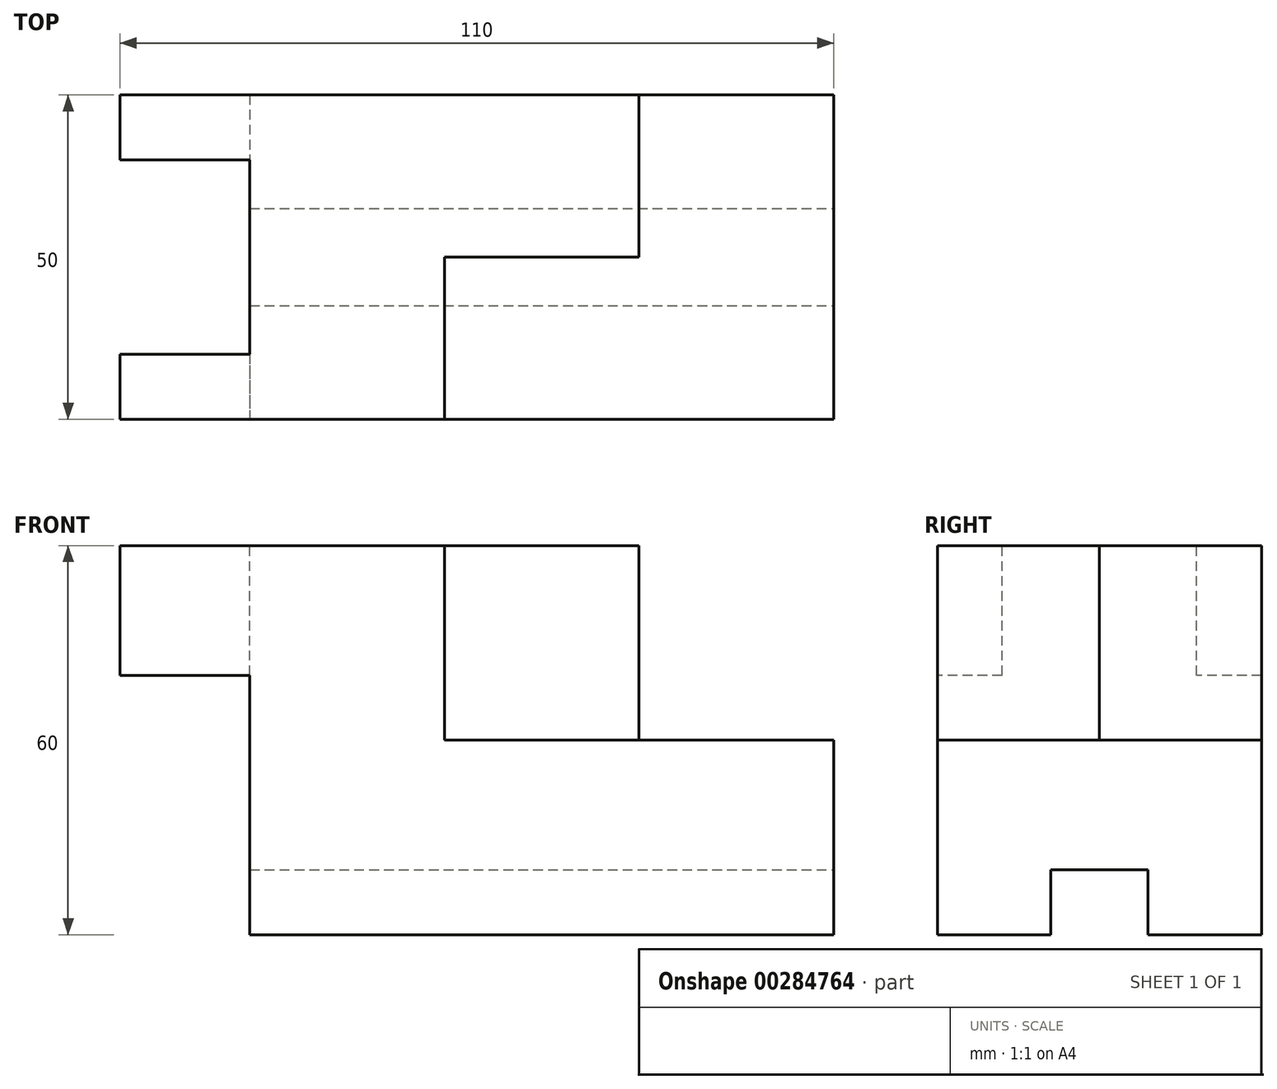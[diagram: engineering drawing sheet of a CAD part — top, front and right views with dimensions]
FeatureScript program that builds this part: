
annotation { "Feature Type Name" : "Feature", "Feature Type Description" : "" }
export const myFeature = defineFeature(function(context is Context, id is Id, definition is map)
    precondition{}
    {
        {
            var Q0;
            Q0=qCreatedBy(makeId("Top.planeOp"),FACE);
            var sketch = newSketch(context, id + "F0", { "sketchPlane" : qUnion([Q0])});
            skLineSegment(sketch, "E0.bottom", {"start": v(-55, -25) * mm, "end": v(55, -25) * mm});
            skLineSegment(sketch, "E0.top", {"start": v(-55, 25) * mm, "end": v(55, 25) * mm});
            skLineSegment(sketch, "E0.left", {"start": v(-55, -25) * mm, "end": v(-55, 25) * mm});
            skLineSegment(sketch, "E0.right", {"start": v(55, -25) * mm, "end": v(55, 25) * mm});
            skPoint(sketch, "E0.middle", {"position": v(0, 0) * mm});
            skSolve(sketch);
        }
        {
            var Q0;
            Q0 = qSketchRegion(id + "F0", true);
            extrude(context, id + "F1", {"entities" : qUnion([Q0]), "depth" : 60 * mm});
        }
        {
            var Q0;
            Q0=makeQuery(id+"F1.opExtrude","SWEPT_FACE",FACE,{"disambiguationData":[OSD([sQuery(id+"F0.wireOp",EDGE,"E0.right")])]});
            var sketch = newSketch(context, id + "F2", { "sketchPlane" : qUnion([Q0])});
            skLineSegment(sketch, "E1.bottom", {"start": v(-7.5, 10) * mm, "end": v(7.5, 10) * mm});
            skLineSegment(sketch, "E1.top", {"start": v(-7.5, -10) * mm, "end": v(7.5, -10) * mm});
            skLineSegment(sketch, "E1.left", {"start": v(-7.5, 10) * mm, "end": v(-7.5, -10) * mm});
            skLineSegment(sketch, "E1.right", {"start": v(7.5, 10) * mm, "end": v(7.5, -10) * mm});
            skPoint(sketch, "E1.middle", {"position": v(0, 0) * mm});
            skSolve(sketch);
        }
        {
            var Q0;
            Q0 = qSketchRegion(id + "F2", true);
            extrude(context, id + "F3", {"entities" : qUnion([Q0]), "operationType" : NewBodyOperationType.REMOVE, "endBound" : BoundingType.THROUGH_ALL, "oppositeDirection" : true, "depth" : 25 * mm});
        }
        {
            var Q0;
            Q0=makeQuery(id+"F1.opExtrude","CAP_FACE",FACE,{"disambiguationData":[OSD([sQuery(id+"F0.wireOp",EDGE,"E0.bottom"),sQuery(id+"F0.wireOp",EDGE,"E0.top"),sQuery(id+"F0.wireOp",EDGE,"E0.left"),sQuery(id+"F0.wireOp",EDGE,"E0.right")])],"isStart":false});
            var sketch = newSketch(context, id + "F4", { "sketchPlane" : qUnion([Q0])});
            skLineSegment(sketch, "E2", {"start": v(25, 25) * mm, "end": v(25, 0) * mm});
            skLineSegment(sketch, "E3", {"start": v(25, 0) * mm, "end": v(-5, 0) * mm});
            skLineSegment(sketch, "E4", {"start": v(-5, 0) * mm, "end": v(-5, -25) * mm});
            skLineSegment(sketch, "E5", {"start": v(-5, -25) * mm, "end": v(55, -25) * mm});
            skLineSegment(sketch, "E6", {"start": v(55, -25) * mm, "end": v(55, 25) * mm});
            skLineSegment(sketch, "E7", {"start": v(25, 25) * mm, "end": v(55, 25) * mm});
            skSolve(sketch);
        }
        {
            var Q0;
            Q0 = qSketchRegion(id + "F4", true);
            extrude(context, id + "F5", {"entities" : qUnion([Q0]), "operationType" : NewBodyOperationType.REMOVE, "oppositeDirection" : true, "depth" : 30 * mm});
        }
        {
            var Q0;
            Q0=makeQuery(id+"F1.opExtrude","SWEPT_FACE",FACE,{"disambiguationData":[OSD([sQuery(id+"F0.wireOp",EDGE,"E0.bottom")])]});
            var sketch = newSketch(context, id + "F6", { "sketchPlane" : qUnion([Q0])});
            skLineSegment(sketch, "E8.bottom", {"start": v(-55, 0) * mm, "end": v(-35, 0) * mm});
            skLineSegment(sketch, "E8.top", {"start": v(-55, 40) * mm, "end": v(-35, 40) * mm});
            skLineSegment(sketch, "E8.left", {"start": v(-55, 0) * mm, "end": v(-55, 40) * mm});
            skLineSegment(sketch, "E8.right", {"start": v(-35, 0) * mm, "end": v(-35, 40) * mm});
            skSolve(sketch);
        }
        {
            var Q0;
            Q0 = qSketchRegion(id + "F6", true);
            extrude(context, id + "F7", {"entities" : qUnion([Q0]), "operationType" : NewBodyOperationType.REMOVE, "endBound" : BoundingType.THROUGH_ALL, "oppositeDirection" : true, "depth" : 25 * mm});
        }
        {
            var Q0;
            Q0=makeQuery(id+"F1.opExtrude","CAP_FACE",FACE,{"disambiguationData":[OSD([sQuery(id+"F0.wireOp",EDGE,"E0.bottom"),sQuery(id+"F0.wireOp",EDGE,"E0.top"),sQuery(id+"F0.wireOp",EDGE,"E0.left"),sQuery(id+"F0.wireOp",EDGE,"E0.right")])],"isStart":false});
            var sketch = newSketch(context, id + "F8", { "sketchPlane" : qUnion([Q0])});
            skLineSegment(sketch, "E9.bottom", {"start": v(-35, 15) * mm, "end": v(-75, 15) * mm});
            skLineSegment(sketch, "E9.top", {"start": v(-35, -15) * mm, "end": v(-75, -15) * mm});
            skLineSegment(sketch, "E9.left", {"start": v(-35, 15) * mm, "end": v(-35, -15) * mm});
            skLineSegment(sketch, "E9.right", {"start": v(-75, 15) * mm, "end": v(-75, -15) * mm});
            skPoint(sketch, "E9.middle", {"position": v(-55, 0) * mm});
            skSolve(sketch);
        }
        {
            var Q0;
            {var subQ0=sQuery(id+"F8.wireOp",EDGE,"E9.left");Q0=makeQuery(id+"F8.imprint","IMPRINT",FACE,{"disambiguationData":[TD([[makeQuery(id+"F8.imprint","IMPRINT",EDGE,{"derivedFrom":subQ0}),-1.0]])]});}
            extrude(context, id + "F9", {"entities" : qUnion([Q0]), "operationType" : NewBodyOperationType.REMOVE, "endBound" : BoundingType.THROUGH_ALL, "oppositeDirection" : true, "depth" : 25 * mm});
        }
    });
